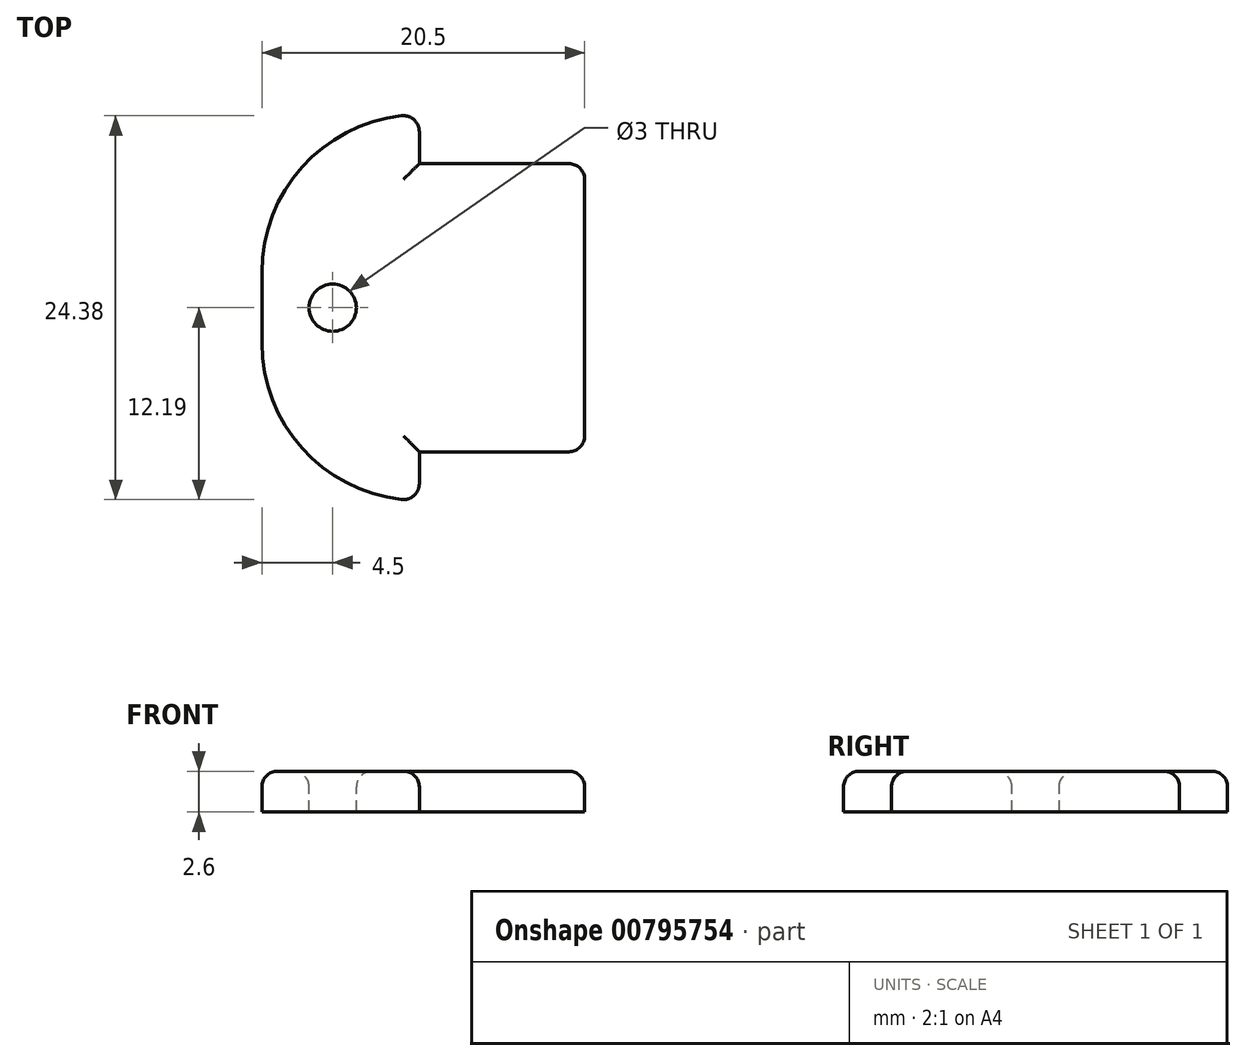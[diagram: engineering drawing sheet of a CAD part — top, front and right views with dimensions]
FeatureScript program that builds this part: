
annotation { "Feature Type Name" : "Feature", "Feature Type Description" : "" }
export const myFeature = defineFeature(function(context is Context, id is Id, definition is map)
    precondition{}
    {
        {
            var Q0;
            Q0=qCreatedBy(makeId("Top.planeOp"),FACE);
            var sketch = newSketch(context, id + "F0", { "sketchPlane" : qUnion([Q0])});
            skLineSegment(sketch, "E0.bottom", {"start": v(5.25, -9.15) * mm, "end": v(-5.25, -9.15) * mm});
            skLineSegment(sketch, "E0.top", {"start": v(5.25, 9.15) * mm, "end": v(-5.25, 9.15) * mm});
            skLineSegment(sketch, "E0.left", {"start": v(5.25, -9.15) * mm, "end": v(5.25, 9.15) * mm});
            skLineSegment(sketch, "E0.right", {"start": v(-5.25, -9.15) * mm, "end": v(-5.25, 9.15) * mm});
            skPoint(sketch, "E0.middle", {"position": v(0, 0) * mm});
            skLineSegment(sketch, "E1.bottom", {"start": v(-5.25, 12.25) * mm, "end": v(-15.25, 12.25) * mm});
            skLineSegment(sketch, "E1.top", {"start": v(-5.25, -12.25) * mm, "end": v(-15.25, -12.25) * mm});
            skLineSegment(sketch, "E1.left", {"start": v(-5.25, 12.25) * mm, "end": v(-5.25, -12.25) * mm});
            skLineSegment(sketch, "E1.right", {"start": v(-15.25, 12.25) * mm, "end": v(-15.25, -12.25) * mm});
            skPoint(sketch, "E1.middle", {"position": v(-10.25, 0) * mm});
            skSolve(sketch);
        }
        {
            var Q0;
            {var subQ0=sQuery(id+"F0.wireOp",EDGE,"E0.bottom");Q0=makeQuery(id+"F0.imprint","IMPRINT",FACE,{"disambiguationData":[TD([[makeQuery(id+"F0.imprint","IMPRINT",EDGE,{"derivedFrom":subQ0}),-1.0]])]});}
            var Q1;
            {var subQ3=sQuery(id+"F0.wireOp",EDGE,"E1.bottom");Q1=makeQuery(id+"F0.imprint","IMPRINT",FACE,{"disambiguationData":[TD([[makeQuery(id+"F0.imprint","IMPRINT",EDGE,{"derivedFrom":subQ3}),1.0]])]});}
            extrude(context, id + "F1", {"entities" : qUnion([Q0, Q1]), "depth" : 2.6 * mm, "offsetDistance" : 25 * mm});
        }
        {
            var Q0;
            Q0=makeQuery(id+"F1.opExtrude","SWEPT_EDGE",EDGE,{"disambiguationData":[OSD([sQuery(id+"F0.wireOp",EDGE,"E1.top"),sQuery(id+"F0.wireOp",EDGE,"E1.right")])]});
            var Q1;
            Q1=makeQuery(id+"F1.opExtrude","SWEPT_EDGE",EDGE,{"disambiguationData":[OSD([sQuery(id+"F0.wireOp",EDGE,"E1.bottom"),sQuery(id+"F0.wireOp",EDGE,"E1.right")])]});
            fillet(context, id + "F2", {"entities" : qUnion([Q0, Q1]), "radius" : 10 * mm, "tangentPropagation" : true, "allowEdgeOverflow" : false});
        }
        {
            var Q0;
            Q0=makeQuery(id+"F1.opExtrude","CAP_FACE",FACE,{"disambiguationData":[OSD([sQuery(id+"F0.wireOp",EDGE,"E0.bottom"),sQuery(id+"F0.wireOp",EDGE,"E0.top"),sQuery(id+"F0.wireOp",EDGE,"E0.left"),sQuery(id+"F0.wireOp",EDGE,"E1.bottom"),sQuery(id+"F0.wireOp",EDGE,"E1.top"),sQuery(id+"F0.wireOp",EDGE,"E1.left"),sQuery(id+"F0.wireOp",EDGE,"E1.right")])],"isStart":false});
            var sketch = newSketch(context, id + "F3", { "sketchPlane" : qUnion([Q0])});
            skCircle(sketch, "E2", {"center": v(-10.75, 0) * mm, "radius": 1.5 * mm});
            skSolve(sketch);
        }
        {
            var Q0;
            Q0=makeQuery(id+"F3.imprint","IMPRINT",FACE,{"disambiguationData":[TD([[makeQuery(id+"F3.imprint","IMPRINT",EDGE,{"derivedFrom":sQuery(id+"F3.wireOp",EDGE,"E2")}),1.0]])]});
            extrude(context, id + "F4", {"entities" : qUnion([Q0]), "operationType" : NewBodyOperationType.REMOVE, "oppositeDirection" : true, "depth" : 25 * mm, "offsetDistance" : 25 * mm});
        }
        {
            var Q0;
            Q0=makeQuery(id+"F1.opExtrude","CAP_FACE",FACE,{"disambiguationData":[OSD([sQuery(id+"F0.wireOp",EDGE,"E0.bottom"),sQuery(id+"F0.wireOp",EDGE,"E0.top"),sQuery(id+"F0.wireOp",EDGE,"E0.left"),sQuery(id+"F0.wireOp",EDGE,"E1.bottom"),sQuery(id+"F0.wireOp",EDGE,"E1.top"),sQuery(id+"F0.wireOp",EDGE,"E1.left"),sQuery(id+"F0.wireOp",EDGE,"E1.right")])],"isStart":false});
            var Q1;
            {var subQ0=sQuery(id+"F0.wireOp",EDGE,"E1.left");var subQ1=sQuery(id+"F0.wireOp",EDGE,"E1.top");Q1=makeQuery(id+"F2.opFillet","BLEND_EDGE",EDGE,{"blendedFrom":[makeQuery(id+"F1.opExtrude","SWEPT_EDGE",EDGE,{"disambiguationData":[OSD([subQ1,sQuery(id+"F0.wireOp",EDGE,"E1.right")])]}),makeQuery(id+"F1.opExtrude","SWEPT_FACE",FACE,{"disambiguationData":[OSD([subQ0]),TDD([makeQuery(id+"F0.imprint","IMPRINT",EDGE,{"disambiguationData":[TD([[makeQuery(id+"F0.imprint","INTERSECT",VERTEX,{"derivedFrom":[sQuery(id+"F0.wireOp",EDGE,"E0.bottom"),subQ0]}),-1.0]])],"derivedFrom":subQ0})])]})],"blendedInto":[makeQuery(id+"F1.opExtrude","SWEPT_FACE",FACE,{"disambiguationData":[OSD([subQ0]),TDD([makeQuery(id+"F0.imprint","IMPRINT",EDGE,{"disambiguationData":[TD([[makeQuery(id+"F0.imprint","INTERSECT",VERTEX,{"derivedFrom":[sQuery(id+"F0.wireOp",EDGE,"E0.bottom"),subQ0]}),-1.0]])],"derivedFrom":subQ0})])]})]});}
            var Q2;
            {var subQ0=sQuery(id+"F0.wireOp",EDGE,"E1.left");var subQ1=sQuery(id+"F0.wireOp",EDGE,"E1.bottom");Q2=makeQuery(id+"F2.opFillet","BLEND_EDGE",EDGE,{"blendedFrom":[makeQuery(id+"F1.opExtrude","SWEPT_EDGE",EDGE,{"disambiguationData":[OSD([subQ1,sQuery(id+"F0.wireOp",EDGE,"E1.right")])]}),makeQuery(id+"F1.opExtrude","SWEPT_FACE",FACE,{"disambiguationData":[OSD([subQ0]),TDD([makeQuery(id+"F0.imprint","IMPRINT",EDGE,{"disambiguationData":[TD([[makeQuery(id+"F0.imprint","INTERSECT",VERTEX,{"derivedFrom":[sQuery(id+"F0.wireOp",EDGE,"E0.top"),subQ0]}),1.0]])],"derivedFrom":subQ0})])]})],"blendedInto":[makeQuery(id+"F1.opExtrude","SWEPT_FACE",FACE,{"disambiguationData":[OSD([subQ0]),TDD([makeQuery(id+"F0.imprint","IMPRINT",EDGE,{"disambiguationData":[TD([[makeQuery(id+"F0.imprint","INTERSECT",VERTEX,{"derivedFrom":[sQuery(id+"F0.wireOp",EDGE,"E0.top"),subQ0]}),1.0]])],"derivedFrom":subQ0})])]})]});}
            var Q3;
            Q3=makeQuery(id+"F1.opExtrude","SWEPT_EDGE",EDGE,{"disambiguationData":[OSD([sQuery(id+"F0.wireOp",EDGE,"E0.top"),sQuery(id+"F0.wireOp",EDGE,"E0.left")])]});
            var Q4;
            Q4=makeQuery(id+"F1.opExtrude","SWEPT_EDGE",EDGE,{"disambiguationData":[OSD([sQuery(id+"F0.wireOp",EDGE,"E0.bottom"),sQuery(id+"F0.wireOp",EDGE,"E0.left")])]});
            fillet(context, id + "F5", {"entities" : qUnion([Q0, Q1, Q2, Q3, Q4]), "radius" : 1 * mm, "tangentPropagation" : true, "allowEdgeOverflow" : false});
        }
    });
